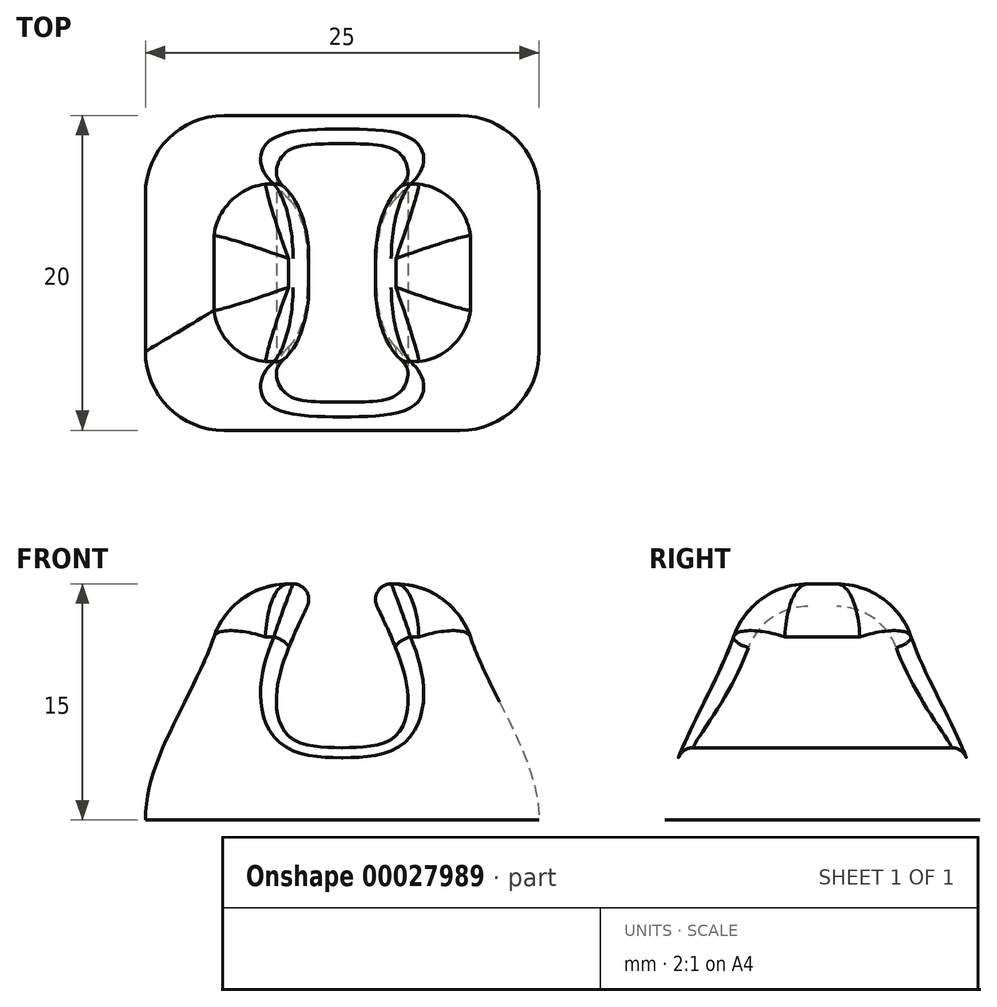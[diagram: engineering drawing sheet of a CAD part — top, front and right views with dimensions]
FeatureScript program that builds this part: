
annotation { "Feature Type Name" : "Feature", "Feature Type Description" : "" }
export const myFeature = defineFeature(function(context is Context, id is Id, definition is map)
    precondition{}
    {
        {
            var Q0;
            Q0=qCreatedBy(makeId("Top.planeOp"),FACE);
            var sketch = newSketch(context, id + "F0", { "sketchPlane" : qUnion([Q0])});
            skLineSegment(sketch, "E0.bottom", {"start": v(5, 0) * mm, "end": v(20, 0) * mm});
            skLineSegment(sketch, "E0.top", {"start": v(5, 20) * mm, "end": v(20, 20) * mm});
            skLineSegment(sketch, "E0.left", {"start": v(0, 5) * mm, "end": v(0, 15) * mm});
            skLineSegment(sketch, "E0.right", {"start": v(25, 5) * mm, "end": v(25, 15) * mm});
            skPoint(sketch, "E1.visualSharp", {"position": v(25, 20) * mm});
            skArc(sketch, "E1.filletArc", {"start": v(25, 15) * mm, "mid": v(23.54, 18.54) * mm, "end": v(20, 20) * mm});
            skPoint(sketch, "E2.visualSharp", {"position": v(0, 20) * mm});
            skArc(sketch, "E2.filletArc", {"start": v(5, 20) * mm, "mid": v(1.46, 18.54) * mm, "end": v(0, 15) * mm});
            skPoint(sketch, "E3.visualSharp", {"position": v(0, 0) * mm});
            skArc(sketch, "E3.filletArc", {"start": v(0, 5) * mm, "mid": v(1.46, 1.46) * mm, "end": v(5, 0) * mm});
            skPoint(sketch, "E4.visualSharp", {"position": v(25, 0) * mm});
            skArc(sketch, "E4.filletArc", {"start": v(20, 0) * mm, "mid": v(23.54, 1.46) * mm, "end": v(25, 5) * mm});
            skLineSegment(sketch, "E5", {"start": v(25, 5) * mm, "end": v(25, 0) * mm, "construction": true});
            skLineSegment(sketch, "E6", {"start": v(0, 5) * mm, "end": v(0, 0) * mm, "construction": true});
            skSolve(sketch);
        }
        {
            var Q0;
            Q0=qCreatedBy(makeId("Top.planeOp"),FACE);
            cPlane(context, id + "F1", {"entities" : qUnion([Q0]), "cplaneType" : CPlaneType.OFFSET, "offset" : 15 * mm, "width" : 150 * mm, "height" : 150 * mm});
        }
        {
            var Q0;
            Q0=qCreatedBy(id+"F1.planeOp",FACE);
            var sketch = newSketch(context, id + "F2", { "sketchPlane" : qUnion([Q0])});
            skLineSegment(sketch, "E7.bottom", {"start": v(8, 15) * mm, "end": v(17, 15) * mm});
            skLineSegment(sketch, "E7.top", {"start": v(8, 5) * mm, "end": v(17, 5) * mm});
            skLineSegment(sketch, "E7.left", {"start": v(5, 12) * mm, "end": v(5, 8) * mm});
            skLineSegment(sketch, "E7.right", {"start": v(20, 12) * mm, "end": v(20, 8) * mm});
            skPoint(sketch, "E8.visualSharp", {"position": v(5, 15) * mm});
            skArc(sketch, "E8.filletArc", {"start": v(8, 15) * mm, "mid": v(5.88, 14.12) * mm, "end": v(5, 12) * mm});
            skPoint(sketch, "E9.visualSharp", {"position": v(5, 5) * mm});
            skArc(sketch, "E9.filletArc", {"start": v(5, 8) * mm, "mid": v(5.88, 5.88) * mm, "end": v(8, 5) * mm});
            skPoint(sketch, "E10.visualSharp", {"position": v(20, 5) * mm});
            skArc(sketch, "E10.filletArc", {"start": v(17, 5) * mm, "mid": v(19.12, 5.88) * mm, "end": v(20, 8) * mm});
            skPoint(sketch, "E11.visualSharp", {"position": v(20, 15) * mm});
            skArc(sketch, "E11.filletArc", {"start": v(20, 12) * mm, "mid": v(19.12, 14.12) * mm, "end": v(17, 15) * mm});
            skSolve(sketch);
        }
        {
            var Q0;
            Q0=makeQuery(id+"F0.imprint","IMPRINT",FACE,{"disambiguationData":[TD([[makeQuery(id+"F0.imprint","IMPRINT",EDGE,{"derivedFrom":sQuery(id+"F0.wireOp",EDGE,"E0.bottom")}),1.0]])]});
            var Q1;
            Q1=makeQuery(id+"F2.imprint","IMPRINT",FACE,{"disambiguationData":[TD([[makeQuery(id+"F2.imprint","IMPRINT",EDGE,{"derivedFrom":sQuery(id+"F2.wireOp",EDGE,"E7.bottom")}),-1.0]])]});
            loft(context, id + "F3", {"startCondition" : LoftEndDerivativeType.NORMAL_TO_PROFILE, "startMagnitude" : 1, "endCondition" : LoftEndDerivativeType.NORMAL_TO_PROFILE, "endMagnitude" : 1, "sheetProfilesArray" : [{ "sheetProfileEntities" : qUnion([Q0]) }, { "sheetProfileEntities" : qUnion([Q1]) }]});
        }
        {
            var Q0;
            Q0=makeQuery(id+"F3.opLoft","CAP_FACE",FACE,{"disambiguationData":[OSD([makeQuery(id+"F2.imprint","IMPRINT",FACE,{"disambiguationData":[TD([[makeQuery(id+"F2.imprint","IMPRINT",EDGE,{"derivedFrom":sQuery(id+"F2.wireOp",EDGE,"E7.bottom")}),-1.0]])]})])],"isStart":true});
            fillet(context, id + "F4", {"entities" : qUnion([Q0]), "radius" : 5 * mm, "tangentPropagation" : true, "allowEdgeOverflow" : false});
        }
        {
            var Q0;
            Q0=qCreatedBy(makeId("Front.planeOp"),FACE);
            var sketch = newSketch(context, id + "F5", { "sketchPlane" : qUnion([Q0])});
            skFitSpline(sketch, "E12", {"points": [v(11, 15) * mm, v(8.32, 7.5) * mm, v(9.3, 5.18) * mm, v(12.5, 4.6) * mm], "startDerivative": vector(-12.35, -24.19) * mm, "endDerivative": vector(12.44, -0.26) * mm});
            skLineSegment(sketch, "E13", {"start": v(0, 0) * mm, "end": v(25, 0) * mm, "construction": true});
            skPoint(sketch, "E14", {"position": v(12.5, 0) * mm});
            skLineSegment(sketch, "E15", {"start": v(12.5, 0) * mm, "end": v(12.5, 15) * mm, "construction": true});
            skLineSegment(sketch, "E16", {"start": v(11, 15) * mm, "end": v(12.5, 15) * mm});
            skLineSegment(sketch, "E17.MirrorCS", {"start": v(14, 15) * mm, "end": v(12.5, 15) * mm});
            skFitSpline(sketch, "E18.MirrorCS", {"points": [v(14, 15) * mm, v(16.68, 7.5) * mm, v(15.7, 5.18) * mm, v(12.5, 4.6) * mm], "startDerivative": vector(12.35, -24.19) * mm, "endDerivative": vector(-12.44, -0.26) * mm});
            skSolve(sketch);
        }
        {
            var Q0;
            Q0=makeQuery(id+"F5.imprint","IMPRINT",FACE,{"disambiguationData":[TD([[makeQuery(id+"F5.imprint","IMPRINT",EDGE,{"derivedFrom":sQuery(id+"F5.wireOp",EDGE,"E12")}),1.0]])]});
            extrude(context, id + "F6", {"entities" : qUnion([Q0]), "operationType" : NewBodyOperationType.REMOVE, "endBound" : BoundingType.THROUGH_ALL, "oppositeDirection" : true, "depth" : 25 * mm});
        }
        {
            var Q0;
            Q0=makeQuery(id+"F6.boolean.opBoolean","COPY",FACE,{"derivedFrom":makeQuery(id+"F6.opExtrude","SWEPT_FACE",FACE,{"disambiguationData":[OSD([sQuery(id+"F5.wireOp",EDGE,"E12")])]})});
            var Q1;
            Q1=makeQuery(id+"F6.boolean.opBoolean","COPY",FACE,{"derivedFrom":makeQuery(id+"F6.opExtrude","SWEPT_FACE",FACE,{"disambiguationData":[OSD([sQuery(id+"F5.wireOp",EDGE,"E18.MirrorCS")])]})});
            fillet(context, id + "F7", {"entities" : qUnion([Q0, Q1]), "radius" : 1 * mm, "tangentPropagation" : true, "allowEdgeOverflow" : false});
        }
    });
